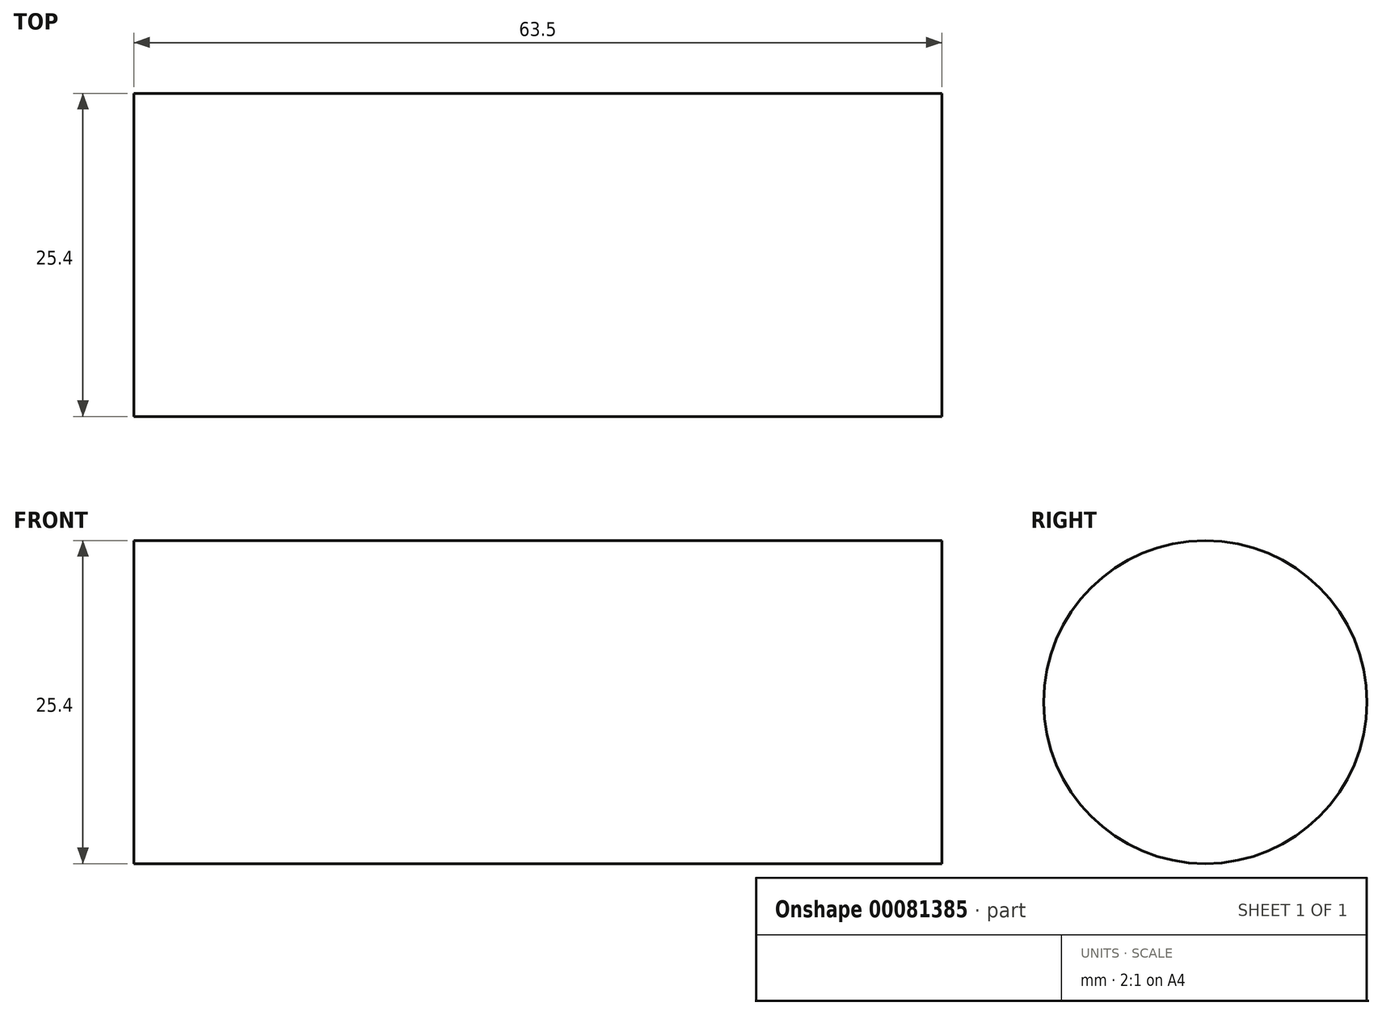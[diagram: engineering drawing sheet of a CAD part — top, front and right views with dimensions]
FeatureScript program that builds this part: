
annotation { "Feature Type Name" : "Feature", "Feature Type Description" : "" }
export const myFeature = defineFeature(function(context is Context, id is Id, definition is map)
    precondition{}
    {
        {
            var Q0;
            Q0=qCreatedBy(makeId("Front.planeOp"),FACE);
            var sketch = newSketch(context, id + "F0", { "sketchPlane" : qUnion([Q0])});
            skLineSegment(sketch, "E0.bottom", {"start": v(0, 0) * mm, "end": v(63.5, 0) * mm});
            skLineSegment(sketch, "E0.top", {"start": v(0, 12.7) * mm, "end": v(63.5, 12.7) * mm});
            skLineSegment(sketch, "E0.left", {"start": v(0, 0) * mm, "end": v(0, 12.7) * mm});
            skLineSegment(sketch, "E0.right", {"start": v(63.5, 0) * mm, "end": v(63.5, 12.7) * mm});
            skLineSegment(sketch, "E1", {"start": v(0, 0) * mm, "end": v(82.92, 0) * mm, "construction": true});
            skSolve(sketch);
        }
        {
            var Q0;
            Q0=makeQuery(id+"F0.imprint","IMPRINT",FACE,{"disambiguationData":[TD([[makeQuery(id+"F0.imprint","IMPRINT",EDGE,{"derivedFrom":sQuery(id+"F0.wireOp",EDGE,"E0.bottom")}),1.0]])]});
            var Q1;
            Q1=sQuery(id+"F0.wireOp",EDGE,"E1");
            revolve(context, id + "F1", {"entities" : qUnion([Q0]), "axis" : qUnion([Q1]), "revolveType" : RevolveType.FULL});
        }
    });
